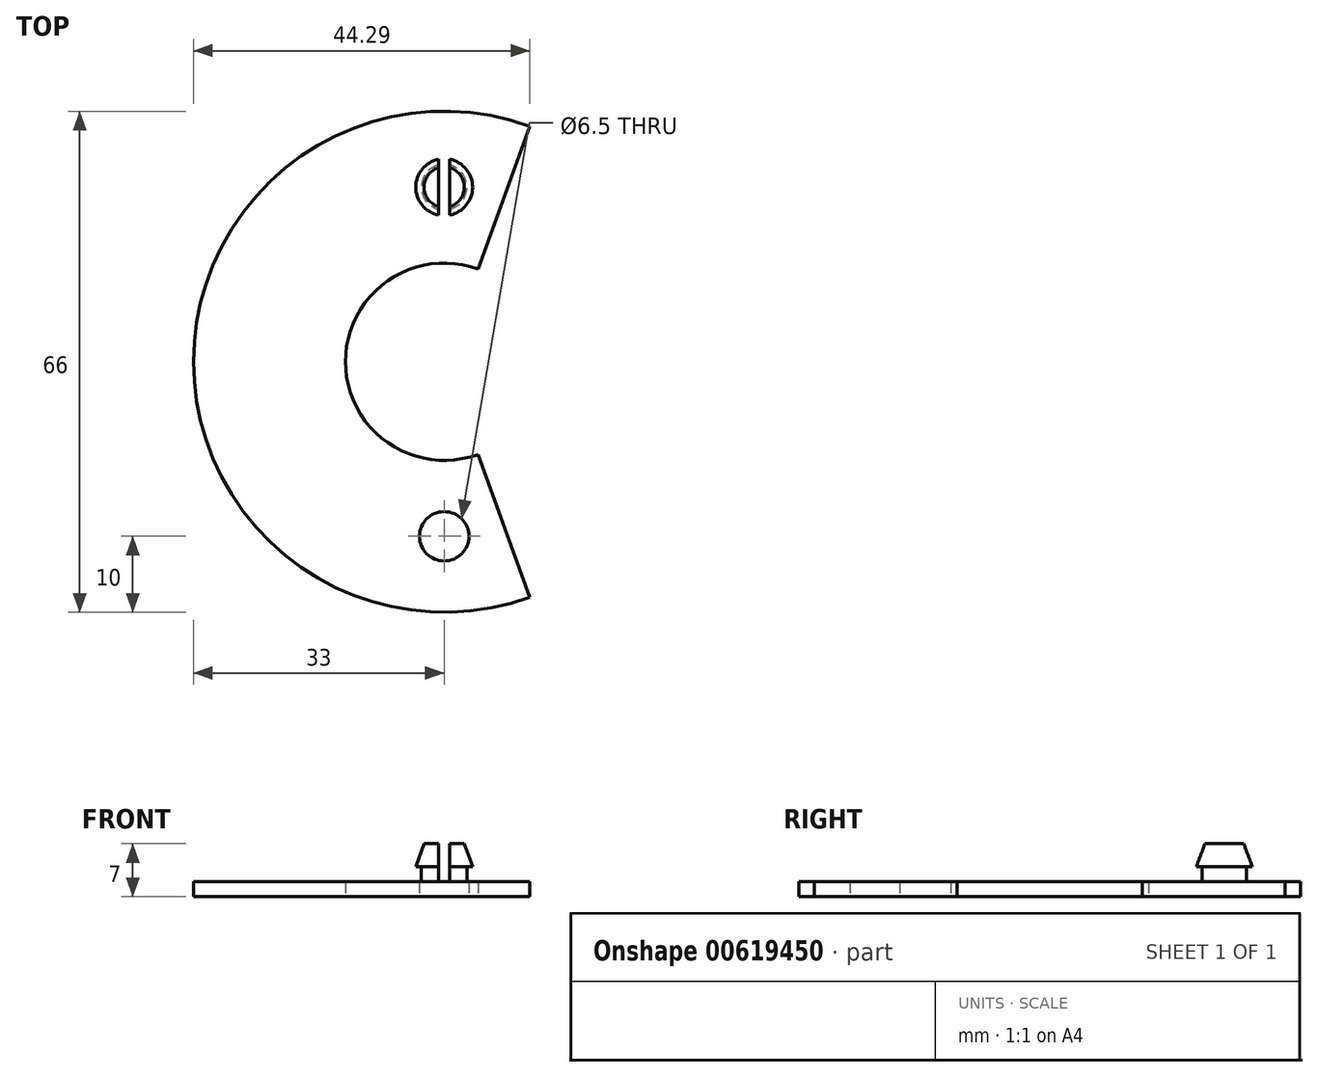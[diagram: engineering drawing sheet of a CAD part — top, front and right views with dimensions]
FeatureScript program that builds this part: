
annotation { "Feature Type Name" : "Feature", "Feature Type Description" : "" }
export const myFeature = defineFeature(function(context is Context, id is Id, definition is map)
    precondition{}
    {
        {
            var Q0;
            Q0=qCreatedBy(makeId("Top.planeOp"),FACE);
            var sketch = newSketch(context, id + "F0", { "sketchPlane" : qUnion([Q0])});
            skArc(sketch, "E0", {"start": v(4.45, 12.22) * mm, "mid": v(-13, 0) * mm, "end": v(4.45, -12.22) * mm});
            skArc(sketch, "E1", {"start": v(11.29, 31) * mm, "mid": v(-33, 0) * mm, "end": v(11.29, -31) * mm});
            skCircle(sketch, "E2", {"center": v(0, 23) * mm, "radius": 3 * mm});
            skCircle(sketch, "E3", {"center": v(0, -23) * mm, "radius": 3.25 * mm});
            skLineSegment(sketch, "E4", {"start": v(0, 13) * mm, "end": v(0, 33) * mm, "construction": true});
            skLineSegment(sketch, "E5", {"start": v(0, -13) * mm, "end": v(0, -33) * mm, "construction": true});
            skLineSegment(sketch, "E6", {"start": v(11.29, -31) * mm, "end": v(4.45, -12.22) * mm});
            skLineSegment(sketch, "E7", {"start": v(4.45, 12.22) * mm, "end": v(11.29, 31) * mm});
            skSolve(sketch);
        }
        {
            var Q0;
            Q0=makeQuery(id+"F0.imprint","IMPRINT",FACE,{"disambiguationData":[TD([[makeQuery(id+"F0.imprint","IMPRINT",EDGE,{"derivedFrom":sQuery(id+"F0.wireOp",EDGE,"E0")}),-1.0]])]});
            extrude(context, id + "F1", {"entities" : qUnion([Q0]), "depth" : 2 * mm, "offsetDistance" : 25 * mm});
        }
        {
            var Q0;
            Q0=makeQuery(id+"F0.imprint","IMPRINT",FACE,{"disambiguationData":[TD([[makeQuery(id+"F0.imprint","IMPRINT",EDGE,{"derivedFrom":sQuery(id+"F0.wireOp",EDGE,"E2")}),1.0]])]});
            extrude(context, id + "F2", {"entities" : qUnion([Q0]), "operationType" : NewBodyOperationType.ADD, "depth" : 4 * mm, "offsetDistance" : 25 * mm});
        }
        {
            var Q0;
            Q0=makeQuery(id+"F2.opExtrude","CAP_FACE",FACE,{"disambiguationData":[OSD([sQuery(id+"F0.wireOp",EDGE,"E2")])],"isStart":false});
            var sketch = newSketch(context, id + "F3", { "sketchPlane" : qUnion([Q0])});
            skCircle(sketch, "E8", {"center": v(0, 23) * mm, "radius": 3.75 * mm});
            skSolve(sketch);
        }
        {
            var Q0;
            Q0=makeQuery(id+"F3.imprint","IMPRINT",FACE,{"disambiguationData":[TD([[makeQuery(id+"F3.imprint","IMPRINT",EDGE,{"derivedFrom":sQuery(id+"F3.wireOp",EDGE,"E8")}),1.0]])]});
            var Q1;
            Q1=makeQuery(id+"F3.imprint","IMPRINT",FACE,{"disambiguationData":[TD([[makeQuery(id+"F3.imprint","IMPRINT",EDGE,{"derivedFrom":makeQuery(id+"F2.opExtrude","CAP_EDGE",EDGE,{"disambiguationData":[OSD([sQuery(id+"F0.wireOp",EDGE,"E2")])],"isStart":false})}),1.0]])]});
            extrude(context, id + "F4", {"entities" : qUnion([Q0, Q1]), "operationType" : NewBodyOperationType.ADD, "depth" : 3 * mm, "offsetDistance" : 25 * mm, "hasDraft" : true, "draftAngle" : 20 * degree, "draftPullDirection" : true});
        }
        {
            var Q0;
            Q0=makeQuery(id+"F4.opExtrude","CAP_FACE",FACE,{"disambiguationData":[OSD([sQuery(id+"F3.wireOp",EDGE,"E8")])],"isStart":false});
            var sketch = newSketch(context, id + "F5", { "sketchPlane" : qUnion([Q0])});
            skLineSegment(sketch, "E9", {"start": v(-0.75, 25.55) * mm, "end": v(-0.75, 20.45) * mm});
            skLineSegment(sketch, "E10", {"start": v(0.75, 20.45) * mm, "end": v(0.75, 25.55) * mm});
            skLineSegment(sketch, "E11", {"start": v(-0.75, 25.55) * mm, "end": v(-0.75, 27.65) * mm});
            skLineSegment(sketch, "E12", {"start": v(0.75, 25.55) * mm, "end": v(0.75, 27.69) * mm});
            skLineSegment(sketch, "E13", {"start": v(-0.75, 20.45) * mm, "end": v(-0.75, 18.7) * mm});
            skLineSegment(sketch, "E14", {"start": v(0.75, 20.45) * mm, "end": v(0.75, 18.73) * mm});
            skLineSegment(sketch, "E15", {"start": v(0.75, 18.73) * mm, "end": v(-0.75, 18.7) * mm});
            skLineSegment(sketch, "E16", {"start": v(-0.75, 27.65) * mm, "end": v(0.75, 27.69) * mm});
            skSolve(sketch);
        }
        {
            var Q0;
            {var subQ0=sQuery(id+"F5.wireOp",EDGE,"E13");Q0=makeQuery(id+"F5.imprint","IMPRINT",FACE,{"disambiguationData":[TD([[makeQuery(id+"F5.imprint","IMPRINT",EDGE,{"derivedFrom":subQ0}),1.0]])]});}
            var Q1;
            {var subQ0=sQuery(id+"F5.wireOp",EDGE,"E9");Q1=makeQuery(id+"F5.imprint","IMPRINT",FACE,{"disambiguationData":[TD([[makeQuery(id+"F5.imprint","IMPRINT",EDGE,{"derivedFrom":subQ0}),1.0]])]});}
            var Q2;
            {var subQ0=sQuery(id+"F5.wireOp",EDGE,"E11");Q2=makeQuery(id+"F5.imprint","IMPRINT",FACE,{"disambiguationData":[TD([[makeQuery(id+"F5.imprint","IMPRINT",EDGE,{"derivedFrom":subQ0}),-1.0]])]});}
            extrude(context, id + "F6", {"entities" : qUnion([Q0, Q1, Q2]), "operationType" : NewBodyOperationType.REMOVE, "oppositeDirection" : true, "depth" : 5 * mm, "offsetDistance" : 25 * mm});
        }
    });
